# Revit family: HVAC_Ductwork_Airzone_Supply-Linear-Diffuser_DFLI-PX_500mm1
name_source: partatom
category: Air Terminals
revit_build: Autodesk Revit 2016 (Build: 20161004_0715(x64)
units: mm (PartAtom-declared; Revit-internal decimal feet)

## family parameters
Always vertical = Yes
Cut with Voids When Loaded = No
OmniClass Number = 23.75.70.21
OmniClass Title = Terminals for Air
Part Type = Normal
Room Calculation Point = Yes
Round Connector Dimension = Use Diameter
Shared = No
Work Plane-Based = No

## types (1)
- INVALID TYPE - Use Load Family and Type Catalog instead
    Accessories Material = Metal - AIRZONE - Aluminium - Satin
    Ak = 0.63
    Compatible Accesories = Plenum for lineal diffuser (PLEN). Linear diffuser corner (DFLIxSQ)
    Description = Linear diffuser
    Disclaimer = All information provided in this model is reviewed before being published. However, Airzone cannot guarantee this model is error-free, therefore users are strongly encouraged to check for technical documentation and updates
    Duct Connection Diameter = 98 mm
    Duct Connection Top Offset = 19 mm
    Duct Diameter = 100 mm
    Duct Height = 75 mm
    Duct Width = 500 mm
    Effective Area = 31.50 cm²
    Finish = White ( RAL 9010)
    Fixing = Fixing bracket. Plenum
    Long Description = Long-range linear diffuser to enable the air supply. 1-4 air outlets. Provided with moving slats, it is designed to be installed in HVAC duct networks. Available in four different models
    Main Material = Metal - AIRZONE - Extruded Aluminium - White (RAL 9010)
    Manufacturer = AIRZONE
    Max Flow = 600 m³/h
    Min Flow = 75 m³/h
    Model = INVALID – Type not loaded via type catalog
    Plenum Center Offset = 20 mm
    Plenum Height = 180 mm
    Plenum Length = 480 mm
    Plenum Material = Metal - AIRZONE - Galvanized Sheet - Semi-polished
    Plenum Width = 83 mm
    Product Code = INVALID – Type not loaded via type catalog
    Product Comments = Refer to technical documentation for further details
    Product Documentation Download URL = http://doc.airzone.es
    Revit Model Version = 1.0
    Type Image Comments = Image available in product documentation download
    URL = www.airzone.es
    c1 = 0.000712
    c2 = -2.073
    c3 = -87.76
    c4 = -37.4
    c5 = 53.51
    c6 = -5.505
    c7 = 0.02769
    c8 = -0.6279

## geometry (parser evidence)
native form markers: Extrusion x2, Sweep x6
no freeform markers — native parametric forms only
